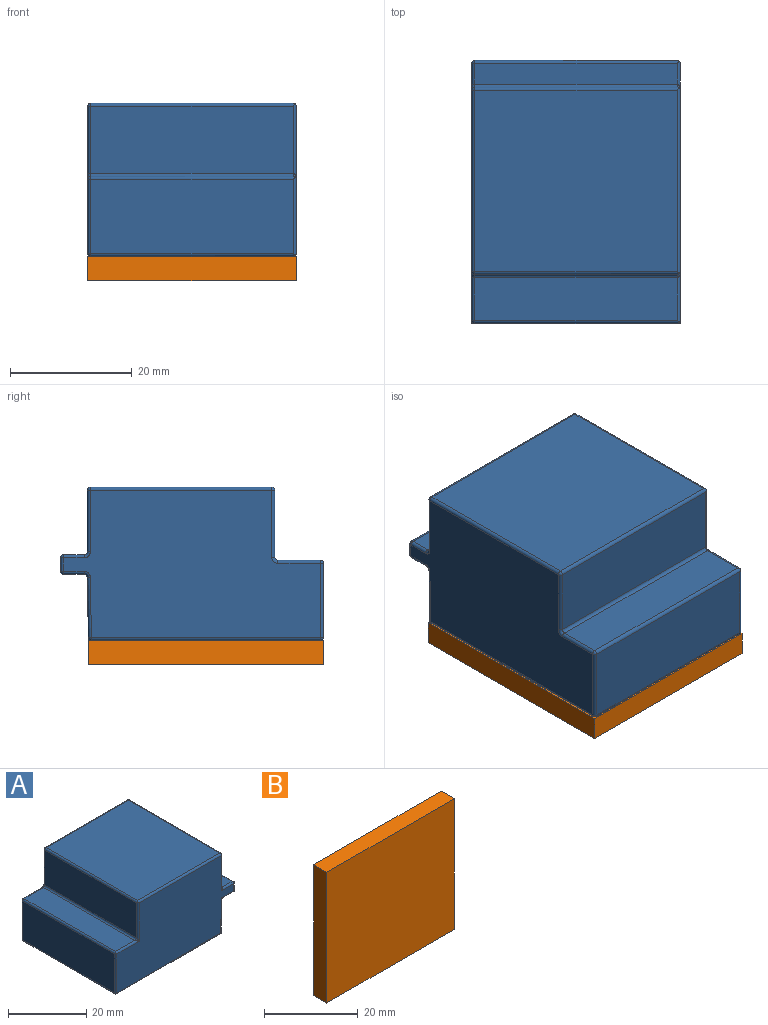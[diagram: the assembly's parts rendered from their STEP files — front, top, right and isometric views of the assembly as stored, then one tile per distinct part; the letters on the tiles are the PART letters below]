
ASSEMBLY  parts=2 mates=1
PART A: 55 faces, bbox 43.2x34.2x25.2 mm
  f0: plane 33.2x9.87mm, normal (1,0,-0.02), area 327.6mm2, adj f17,f45,f51,f54
  f1: plane 33.2x3.41mm, normal (0,0,-1), area 113.2mm2, adj f15,f38,f45,f46
  f2: plane 33.2x2.25mm, normal (1,0,0), area 74.7mm2, adj f13,f32,f38,f39
  f3: plane 33.2x3.4mm, normal (0,0,1), area 112.9mm2, adj f12,f25,f32,f33
  f4: plane 33.2x10.1mm, normal (1,0,0), area 335.3mm2, adj f14,f22,f25,f26
  f5: plane 33.2x29.78mm, normal (0,0,1), area 988.6mm2, adj f16,f22,f27,f28
  f6: plane 33.2x11mm, normal (-1,0,0), area 365.2mm2, adj f18,f28,f34,f35
  f7: plane 33.2x7mm, normal (0,0,1), area 232.4mm2, adj f20,f35,f40,f41
  f8: plane 33.2x12.2mm, normal (-1,0,0), area 405mm2, adj f21,f41,f47,f48
  f9: plane 37.61x33.2mm, normal (0,0,-1), area 1248.6mm2, adj f19,f48,f52,f54
  f10: plane 42.18x24.2mm, normal (0,-1,0), area 827.3mm2, adj f12,f13,f14,f15,f16,f17,f18,f19
  f11: plane 42.18x24.2mm, normal (0,1,0), area 827.9mm2, adj f26,f27,f29,f33,f34,f37,f39,f40
  f12: cylinder r=0.5mm len=4.75mm, axis (1,0,0), area 3.1mm2, adj f3,f10,f13,f23,f32
  f13: cylinder r=0.5mm len=2.96mm, axis (0,0,-1), area 2.1mm2, adj f2,f10,f12,f15,f32,f38
  f14: cylinder r=0.5mm len=11.45mm, axis (0,0,-1), area 8.4mm2, adj f4,f10,f16,f22,f23
  f15: cylinder r=0.5mm len=4.75mm, axis (-1,0,0), area 3.1mm2, adj f1,f10,f13,f38,f42
  f16: cylinder r=0.5mm len=30.49mm, axis (1,0,0), area 23.7mm2, adj f5,f10,f14,f18,f22,f28
  f17: cylinder r=0.5mm len=11.21mm, axis (-0.02,0,-1), area 8.2mm2, adj f0,f10,f19,f42,f54
  f18: cylinder r=0.5mm len=12.35mm, axis (0,0,1), area 9.1mm2, adj f6,f10,f16,f28,f31
  f19: cylinder r=0.5mm len=38.31mm, axis (-1,0,0), area 29.8mm2, adj f9,f10,f17,f21,f48,f54
  f20: cylinder r=0.5mm len=8.35mm, axis (1,0,0), area 5.9mm2, adj f7,f10,f21,f31,f41
  f21: cylinder r=0.5mm len=12.91mm, axis (0,0,1), area 9.9mm2, adj f8,f10,f19,f20,f41,f48
  f22: cylinder r=0.5mm len=33.55mm, axis (0,1,0), area 26.2mm2, adj f4,f5,f14,f16,f24
  f23: bspline ~1x1mm, area 0.5mm2, adj f12,f14,f25
  f24: sphere r=0.5mm, area 0.4mm2, adj f22,f26,f27
  f25: cylinder r=0.5mm len=33.2mm, axis (0,-1,0), area 26.1mm2, adj f3,f4,f23,f29
  f26: cylinder r=0.5mm len=10.1mm, axis (0,0,1), area 7.9mm2, adj f4,f11,f24,f29
  f27: cylinder r=0.5mm len=29.78mm, axis (-1,0,0), area 23.4mm2, adj f5,f11,f24,f30
  f28: cylinder r=0.5mm len=33.55mm, axis (0,1,0), area 26.2mm2, adj f5,f6,f16,f18,f30
  f29: torus R=1mm, axis (0,-1,0), area 0.8mm2, adj f11,f25,f26,f33
  f30: sphere r=0.5mm, area 0.4mm2, adj f27,f28,f34
  f31: bspline ~1x1mm, area 0.5mm2, adj f18,f20,f35
  f32: cylinder r=0.5mm len=33.55mm, axis (0,1,0), area 26.2mm2, adj f2,f3,f12,f13,f36
  f33: cylinder r=0.5mm len=3.4mm, axis (-1,0,0), area 2.7mm2, adj f3,f11,f29,f36
  f34: cylinder r=0.5mm len=11mm, axis (0,0,-1), area 8.6mm2, adj f6,f11,f30,f37
  f35: cylinder r=0.5mm len=33.2mm, axis (0,-1,0), area 26.1mm2, adj f6,f7,f31,f37
  f36: sphere r=0.5mm, area 0.4mm2, adj f32,f33,f39
  f37: torus R=1mm, axis (0,-1,0), area 0.8mm2, adj f11,f34,f35,f40
  f38: cylinder r=0.5mm len=33.55mm, axis (0,1,0), area 26.2mm2, adj f1,f2,f13,f15,f43
  f39: cylinder r=0.5mm len=2.25mm, axis (0,0,1), area 1.8mm2, adj f2,f11,f36,f43
  f40: cylinder r=0.5mm len=7mm, axis (-1,0,0), area 5.5mm2, adj f7,f11,f37,f44
  f41: cylinder r=0.5mm len=33.55mm, axis (0,1,0), area 26.2mm2, adj f7,f8,f20,f21,f44
  f42: bspline ~0.99x0.98mm, area 0.5mm2, adj f15,f17,f45
  f43: sphere r=0.5mm, area 0.4mm2, adj f38,f39,f46
  f44: sphere r=0.5mm, area 0.4mm2, adj f40,f41,f47
  f45: cylinder r=0.5mm len=33.2mm, axis (0,-1,0), area 25.8mm2, adj f0,f1,f42,f49
  f46: cylinder r=0.5mm len=3.41mm, axis (1,0,0), area 2.7mm2, adj f1,f11,f43,f49
  f47: cylinder r=0.5mm len=12.2mm, axis (0,0,-1), area 9.6mm2, adj f8,f11,f44,f50
  f48: cylinder r=0.5mm len=33.55mm, axis (0,-1,0), area 26.2mm2, adj f8,f9,f19,f21,f50
  f49: torus R=1mm, axis (0,-1,0), area 0.8mm2, adj f11,f45,f46,f51
  f50: sphere r=0.5mm, area 0.4mm2, adj f47,f48,f52
  f51: cylinder r=0.5mm len=9.87mm, axis (0.02,0,1), area 7.8mm2, adj f0,f11,f49,f53
  f52: cylinder r=0.5mm len=37.61mm, axis (1,0,0), area 29.5mm2, adj f9,f11,f50,f53
  f53: sphere r=0.5mm, area 0.4mm2, adj f51,f52,f54
  f54: cylinder r=0.5mm len=33.55mm, axis (0,-1,0), area 25.9mm2, adj f0,f9,f17,f19,f53
PART B: 6 faces, bbox 38.6x4x34.2 mm
  f0: plane 38.6x4mm, normal (0,0,1), area 154.4mm2, adj f1,f3,f4,f5
  f1: plane 34.2x4mm, normal (-1,0,0), area 136.8mm2, adj f0,f2,f4,f5
  f2: plane 38.6x4mm, normal (0,0,-1), area 154.4mm2, adj f1,f3,f4,f5
  f3: plane 34.2x4mm, normal (1,0,0), area 136.8mm2, adj f0,f2,f4,f5
  f4: plane 38.6x34.2mm, normal (0,-1,0), area 1320.1mm2, adj f0,f1,f2,f3
  f5: plane 38.6x34.2mm, normal (0,1,0), area 1320.1mm2, adj f0,f1,f2,f3
PLACE A rot(axis=(0,0,1),90deg) t=(-18.69,-39.58,-14.33)mm
PLACE B rot(axis=(-0.58,-0.58,0.58),120deg) t=(-1.59,-20.27,-18.33)mm
MATE fastened A.f9 <-> B.f4  axis (0,0,-1) through (-1.59,-20.27,-14.33)mm
